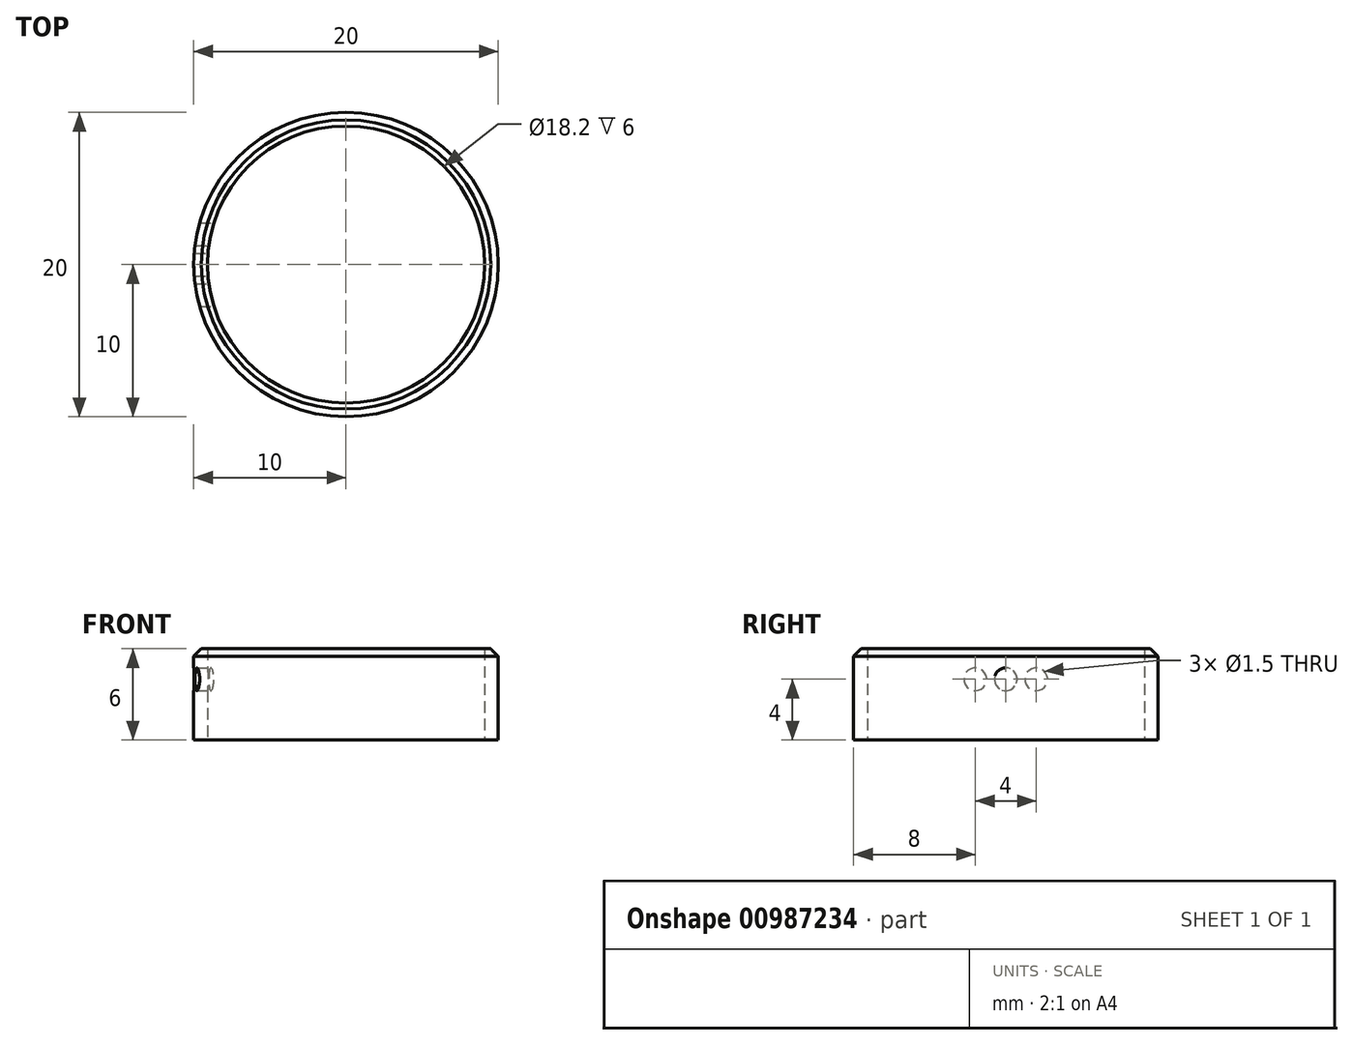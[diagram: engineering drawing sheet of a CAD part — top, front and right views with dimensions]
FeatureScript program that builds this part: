
annotation { "Feature Type Name" : "Feature", "Feature Type Description" : "" }
export const myFeature = defineFeature(function(context is Context, id is Id, definition is map)
    precondition{}
    {
        {
            var Q0;
            Q0=qCreatedBy(makeId("Top.planeOp"),FACE);
            var sketch = newSketch(context, id + "F0", { "sketchPlane" : qUnion([Q0])});
            skCircle(sketch, "E0", {"center": v(0, 0) * mm, "radius": 10 * mm});
            skCircle(sketch, "E1", {"center": v(0, 0) * mm, "radius": 9.1 * mm});
            skSolve(sketch);
        }
        {
            var Q0;
            Q0=makeQuery(id+"F0.imprint","IMPRINT",FACE,{"disambiguationData":[TD([[makeQuery(id+"F0.imprint","IMPRINT",EDGE,{"derivedFrom":sQuery(id+"F0.wireOp",EDGE,"E0")}),1.0]])]});
            extrude(context, id + "F1", {"entities" : qUnion([Q0]), "depth" : 6 * mm, "offsetDistance" : 25 * mm});
        }
        {
            var Q0;
            Q0=qCreatedBy(makeId("Right.planeOp"),FACE);
            var sketch = newSketch(context, id + "F2", { "sketchPlane" : qUnion([Q0])});
            skLineSegment(sketch, "E2", {"start": v(0, 0) * mm, "end": v(0, 4) * mm});
            skLineSegment(sketch, "E3", {"start": v(2, 4) * mm, "end": v(-2, 4) * mm});
            skCircle(sketch, "E4", {"center": v(2, 4) * mm, "radius": 0.75 * mm});
            skCircle(sketch, "E5", {"center": v(-2, 4) * mm, "radius": 0.75 * mm});
            skCircle(sketch, "E6", {"center": v(0, 4) * mm, "radius": 0.75 * mm});
            skSolve(sketch);
        }
        {
            var Q0;
            Q0=makeQuery(id+"F2.imprint","IMPRINT",FACE,{"disambiguationData":[TD([[makeQuery(id+"F2.imprint","IMPRINT",EDGE,{"derivedFrom":sQuery(id+"F2.wireOp",EDGE,"E4")}),1.0]])]});
            var Q1;
            {var subQ0=sQuery(id+"F2.wireOp",EDGE,"E3");var subQ1=sQuery(id+"F2.wireOp",EDGE,"E2");var subQ2=makeQuery(id+"F2.imprint","INTERSECT",VERTEX,{"derivedFrom":[subQ1,subQ0]});Q1=makeQuery(id+"F2.imprint","IMPRINT",FACE,{"disambiguationData":[TD([[makeQuery(id+"F2.imprint","IMPRINT",EDGE,{"disambiguationData":[TD([[subQ2,1.0]])],"derivedFrom":subQ1}),-1.0]])]});}
            var Q2;
            {var subQ0=sQuery(id+"F2.wireOp",EDGE,"E3");var subQ1=makeQuery(id+"F2.imprint","INTERSECT",VERTEX,{"derivedFrom":[sQuery(id+"F2.wireOp",EDGE,"E2"),subQ0]});Q2=makeQuery(id+"F2.imprint","IMPRINT",FACE,{"disambiguationData":[TD([[makeQuery(id+"F2.imprint","IMPRINT",EDGE,{"disambiguationData":[TD([[subQ1,1.0]])],"derivedFrom":subQ0}),-1.0]])]});}
            var Q3;
            {var subQ0=sQuery(id+"F2.wireOp",EDGE,"E3");var subQ1=sQuery(id+"F2.wireOp",EDGE,"E2");var subQ2=makeQuery(id+"F2.imprint","INTERSECT",VERTEX,{"derivedFrom":[subQ1,subQ0]});Q3=makeQuery(id+"F2.imprint","IMPRINT",FACE,{"disambiguationData":[TD([[makeQuery(id+"F2.imprint","IMPRINT",EDGE,{"disambiguationData":[TD([[subQ2,1.0]])],"derivedFrom":subQ1}),1.0]])]});}
            var Q4;
            Q4=makeQuery(id+"F2.imprint","IMPRINT",FACE,{"disambiguationData":[TD([[makeQuery(id+"F2.imprint","IMPRINT",EDGE,{"derivedFrom":sQuery(id+"F2.wireOp",EDGE,"E5")}),1.0]])]});
            extrude(context, id + "F3", {"entities" : qUnion([Q0, Q1, Q2, Q3, Q4]), "operationType" : NewBodyOperationType.REMOVE, "oppositeDirection" : true, "depth" : 25 * mm, "offsetDistance" : 25 * mm});
        }
        {
            var Q0;
            Q0=makeQuery(id+"F1.opExtrude","CAP_EDGE",EDGE,{"disambiguationData":[OSD([sQuery(id+"F0.wireOp",EDGE,"E0")])],"isStart":false});
            chamfer(context, id + "F4", {"entities" : qUnion([Q0]), "width" : .5 * mm, "tangentPropagation" : true});
        }
    });
